# Revit family: ledspotra-slim-e_7w-927_930_940-dim-bl_541003767600_33af
name_source: partatom
category: Lighting Fixtures
units: mm (PartAtom-declared; Revit-internal decimal feet)

## family parameters
Cut with Voids When Loaded = No
Host = Face
Light Source = No
Part Type = Normal
Room Calculation Point = No
Round Connector Dimension = Use Diameter
Shared = No

## types (1)
- LEDSpotRA-Slim-E 7W-927/930/940-DIM-BL (1 x LED, 735 lm, 4000)
    Apparent Load = 8 VA
    Approval mark = CE
    CIE Flux Codes = 88 98 100 100 100
    Color Rendering = 90
    Color Temperature = 4000
    Control Gear = Electronic ballast
    Default Elevation = 1800 mm
    Description = Slim Spot EcoMax Ø85mm-8W-735lm-3/4000K-36°-Triac-Black
    Frequency = 60 Hz
    Height = 0 mm  [stored 0 ft]
    Lamp = 1 x LED
    Lamp Light Flux = 735 lm
    Lamp count = 1
    Length = 85 mm
    Luminous efficacy = 92 lm/W
    Manufacturer = OPPLE
    ModVariant = No
    Model = 541003767600
    Mounting Place = Ceiling
    Mounting Type = Recessed
    Number of Poles = 1
    OnlyDefault = Yes
    Power Factor = 1
    Product Name = LEDSpotRA-Slim-E 7W-927/930/940-DIM-BL
    Product group = Spot EcoMax
    ProductGroupID = 420
    Protection Class = Protection class II
    Protection Degree = IP 20
    RLX_Detail_Level = 1
    RLX_Emergency_Light_Flux = 0 lm
    RLX_Emergency_Type = 0
    RLX_Emergency_Type_DB = No
    RlxData = <blob elided: 184657 chars, md5=d16f275c>
    Socket = socket
    Standby Power = 0 W
    System Light Flux = 735 lm
    System Power = 8 W
    Type Comments = Product without accessories
    Type Image = web_spot_slim_bl.jpg
    URL = http://relux.com
    VarID = ---
    Voltage = 230 V
    Voltage Range = 220-240 V
    Weight = 0.00 kg
    Width = 85 mm

note: [stored X ft] marks values corroborated as IEEE doubles in the binary element streams (Revit-internal decimal feet)

## geometry (parser evidence)
native form markers: Sweep x13
no freeform markers — native parametric forms only
